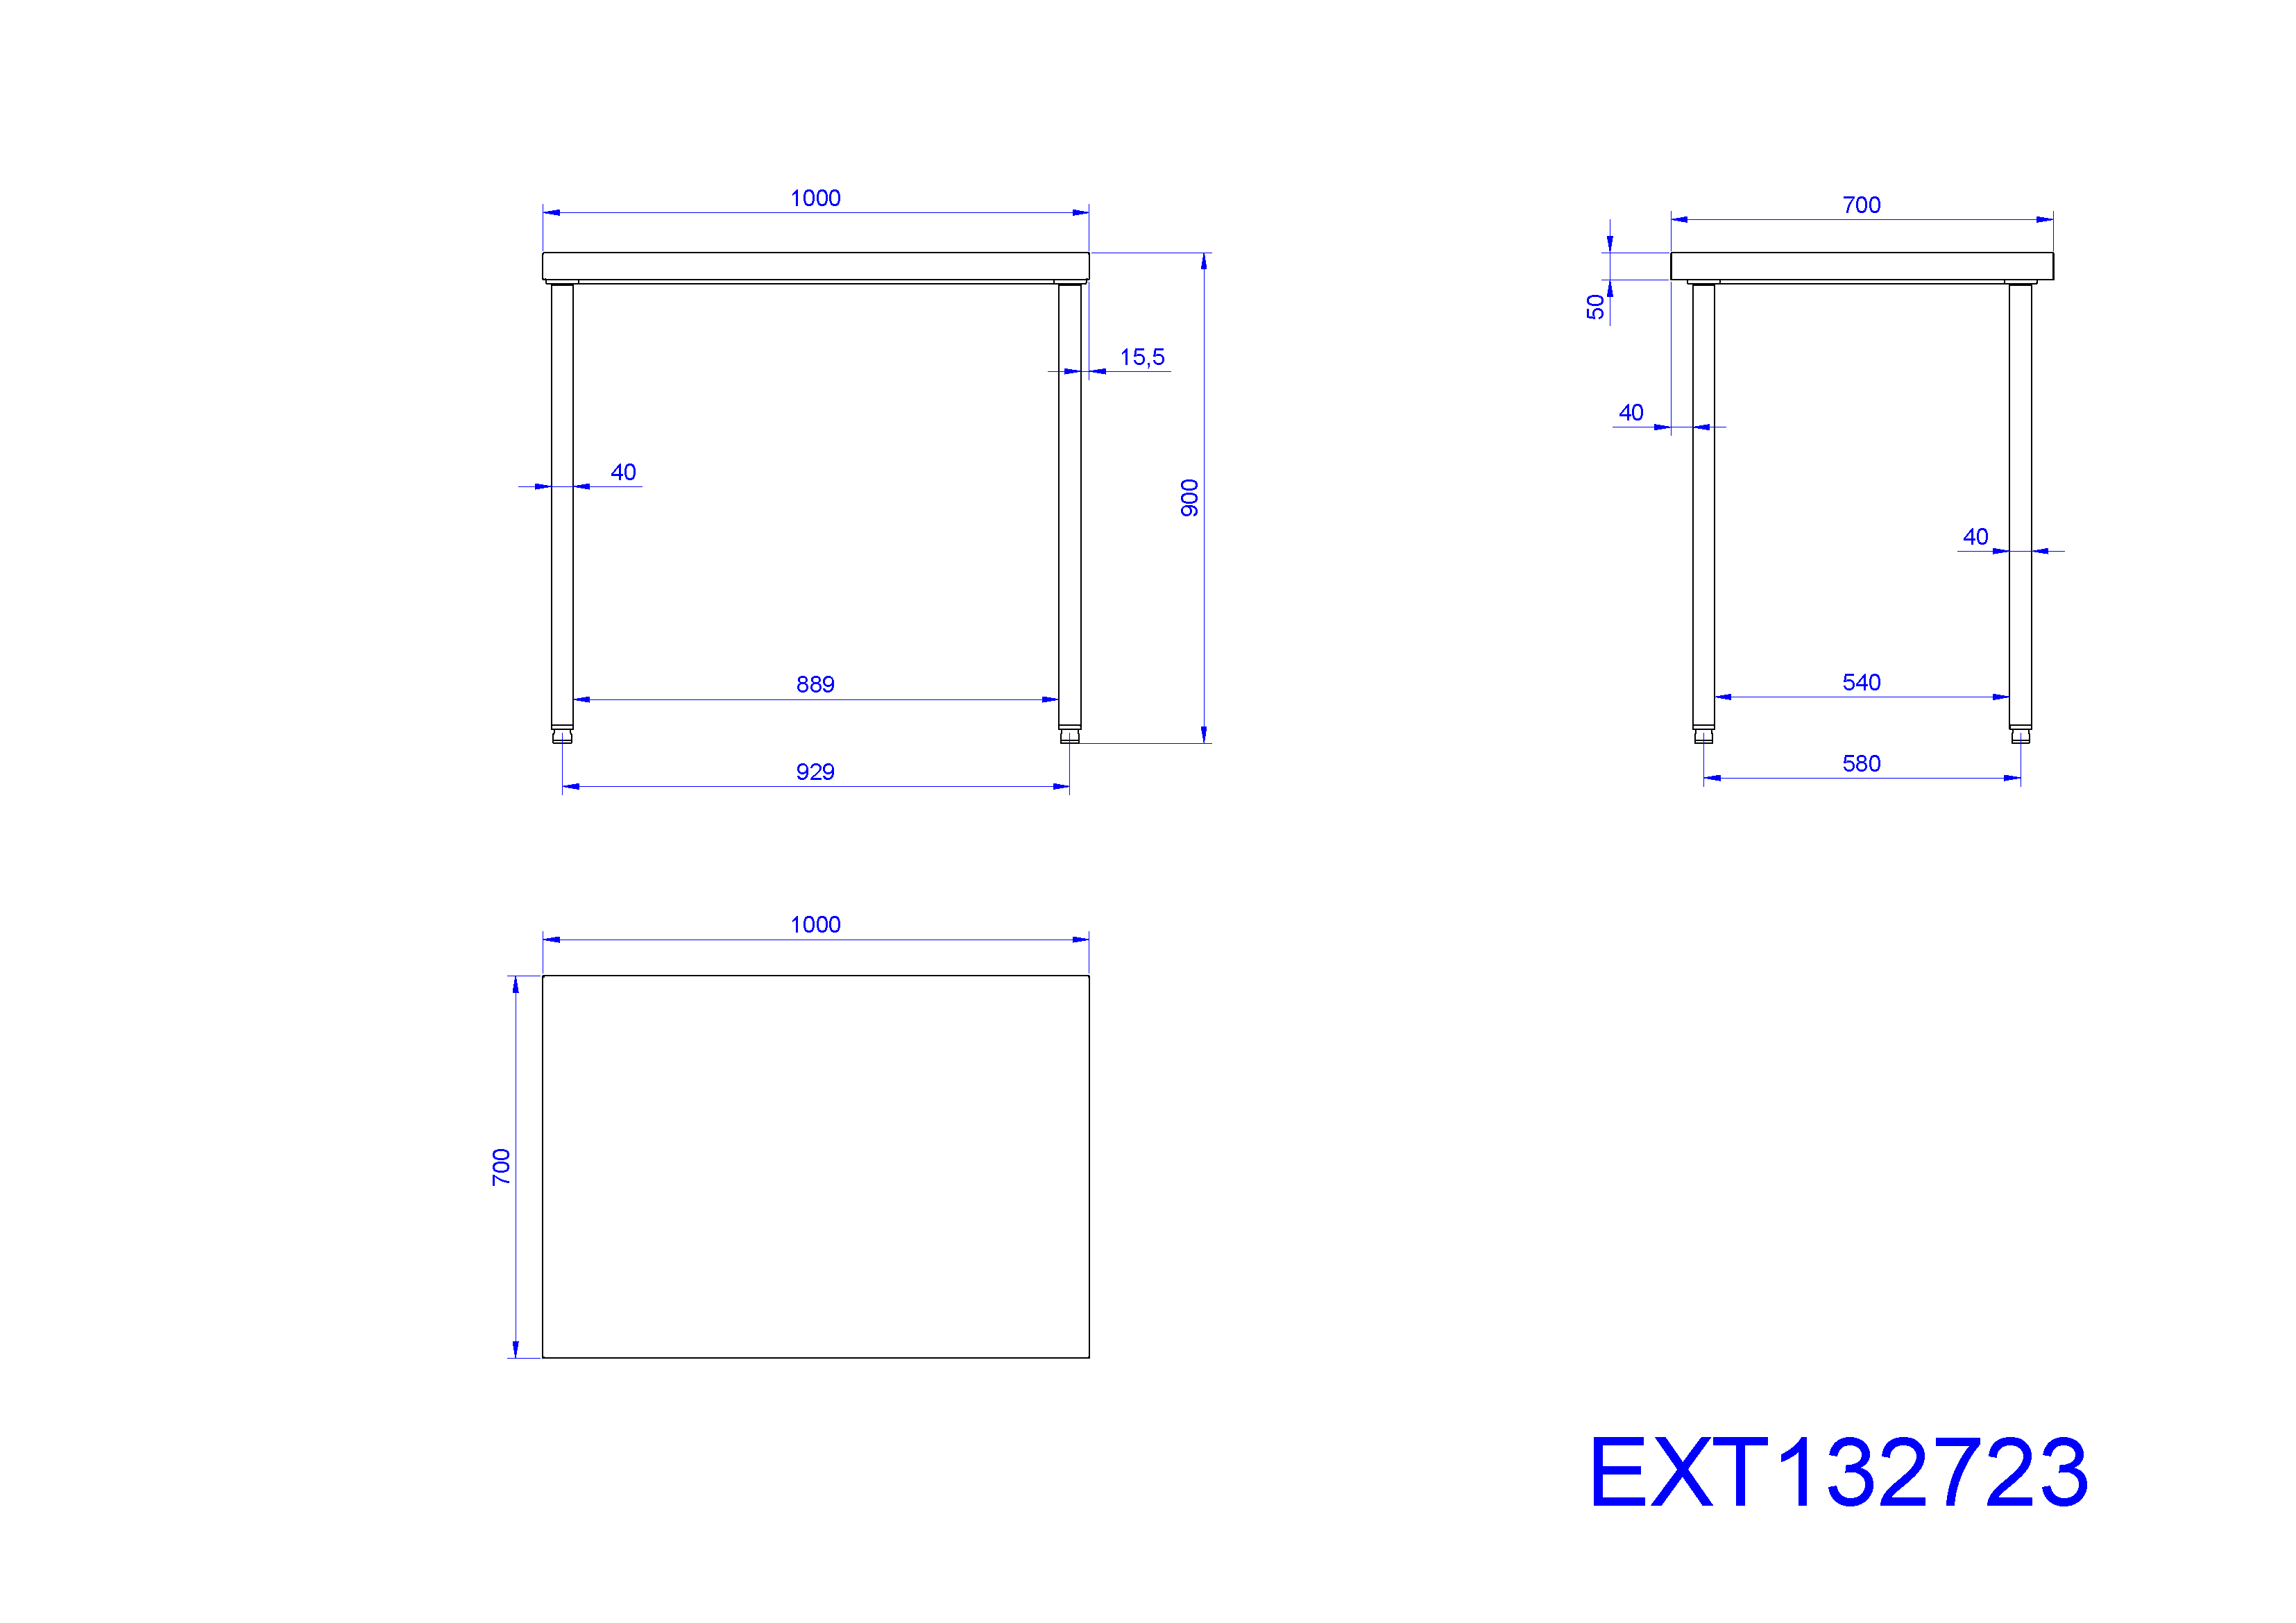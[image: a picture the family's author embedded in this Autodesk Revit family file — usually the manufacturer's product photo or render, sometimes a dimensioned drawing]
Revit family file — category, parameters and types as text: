
# Revit family: QF_ELECTROLUXPROFESSIONAL_133053_TG2000EN
name_source: partatom
category: Attrezzature speciali
units: mm (PartAtom-declared; Revit-internal decimal feet)

## family parameters
Basato su piano di lavoro = No
Condiviso = No
Punto di calcolo locali = No
Quota connettore circolare = Usa diametro
Sempre verticale = Sì
Taglio con vuoti quando caricato = No
Tipo di parte = Normale

## types (1)
- Standard
    Accessory = Sì
    Cold Water Size = 0 mm
    Compressed Air Pressure = 0.0 Pa
    Compressed Air Size = 0 mm
    Compressed Air Volume = 0.0 L/s
    Condensate Return Size = 0 mm
    Cycle = 0 Hz
    Depth Actual = 700 mm  [stored 2.29659 ft]
    Descrizione = WORK TABLE 2000 MM
    Direct Waste Size = 0 mm
    Gas Input Pressure = 0
    Gas KW = 0
    Gas Size = 0 mm
    HP = 0 HP
    Height Actual = 900 mm  [stored 2.95276 ft]
    Hot Water Size = 0 mm
    Item Number = 133053
    Length Actual = 2000 mm  [stored 6.56168 ft]
    Modello = TG2000EN
    Phase = 0
    Produttore = Electrolux Professional
    Prospetto di default = 0 mm  [stored 0 ft]
    Refrigerant Compressor Remote = Sì
    Refrigeration Liquid Line Size = 0 mm  [stored 0 ft]
    Refrigeration Suction Line Size = 0 mm  [stored 0 ft]
    Steam Consumption per Hour = 0
    Steam Supply Maximum Pressure = 0.0 Pa
    Steam Supply Minimum Pressure = 0.0 Pa
    Steam Supply Size = 0 mm
    URL = https://www.electroluxprofessional.com
    URL Manufacturer = https://www.electroluxprofessional.com
    Volts = 0 V
    Watts = 0 W
    Weight = 58.00 kg

note: source unit labels omitted for Gas Input Pressure — the stored unit's dimension contradicts the parameter name (converter mislabeling)

note: [stored X ft] marks values corroborated as IEEE doubles in the binary element streams (Revit-internal decimal feet)

## geometry (parser evidence)
native form markers: Sweep x2
no freeform markers — native parametric forms only
